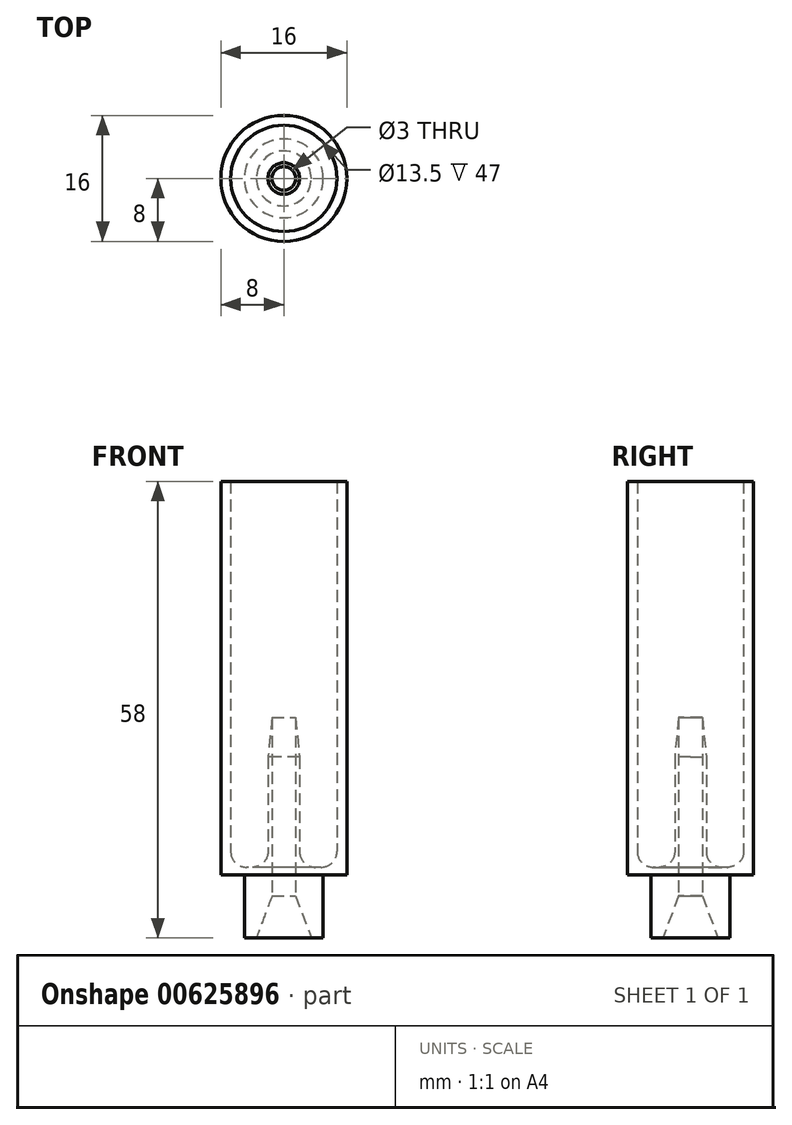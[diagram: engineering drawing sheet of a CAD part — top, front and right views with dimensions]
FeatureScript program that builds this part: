
annotation { "Feature Type Name" : "Feature", "Feature Type Description" : "" }
export const myFeature = defineFeature(function(context is Context, id is Id, definition is map)
    precondition{}
    {
        {
            var Q0;
            Q0=qCreatedBy(makeId("Top.planeOp"),FACE);
            var sketch = newSketch(context, id + "F0", { "sketchPlane" : qUnion([Q0])});
            skCircle(sketch, "E0", {"center": v(0, 0) * mm, "radius": 5 * mm});
            skCircle(sketch, "E1", {"center": v(0, 0) * mm, "radius": 3.5 * mm});
            skSolve(sketch);
        }
        {
            var Q0;
            Q0=makeQuery(id+"F0.imprint","IMPRINT",FACE,{"disambiguationData":[TD([[makeQuery(id+"F0.imprint","IMPRINT",EDGE,{"derivedFrom":sQuery(id+"F0.wireOp",EDGE,"E0")}),1.0]])]});
            extrude(context, id + "F1", {"entities" : qUnion([Q0]), "depth" : 8 * mm, "offsetDistance" : 25 * mm});
        }
        {
            var Q0;
            Q0=makeQuery(id+"F1.opExtrude","CAP_FACE",FACE,{"disambiguationData":[OSD([sQuery(id+"F0.wireOp",EDGE,"E0"),sQuery(id+"F0.wireOp",EDGE,"E1")])],"isStart":false});
            var sketch = newSketch(context, id + "F2", { "sketchPlane" : qUnion([Q0])});
            skCircle(sketch, "E2", {"center": v(0, 0) * mm, "radius": 8 * mm});
            skCircle(sketch, "E3", {"center": v(0, 0) * mm, "radius": 2 * mm});
            skCircle(sketch, "E4", {"center": v(0, 0) * mm, "radius": 1.5 * mm});
            skCircle(sketch, "E5", {"center": v(0, 0) * mm, "radius": 6.75 * mm});
            skSolve(sketch);
        }
        {
            var Q0;
            Q0 = qSketchRegion(id + "F2", true);
            var Q1;
            Q1=makeQuery(id+"F2.imprint","IMPRINT",FACE,{"disambiguationData":[TD([[makeQuery(id+"F2.imprint","IMPRINT",EDGE,{"derivedFrom":sQuery(id+"F2.wireOp",EDGE,"E5")}),1.0]])]});
            var Q2;
            Q2=makeQuery(id+"F2.imprint","IMPRINT",FACE,{"disambiguationData":[TD([[makeQuery(id+"F2.imprint","IMPRINT",EDGE,{"derivedFrom":makeQuery(id+"F1.opExtrude","CAP_EDGE",EDGE,{"disambiguationData":[OSD([sQuery(id+"F0.wireOp",EDGE,"E0")])],"isStart":false})}),1.0]])]});
            var Q3;
            Q3=makeQuery(id+"F2.imprint","IMPRINT",FACE,{"disambiguationData":[TD([[makeQuery(id+"F2.imprint","IMPRINT",EDGE,{"derivedFrom":sQuery(id+"F2.wireOp",EDGE,"E3")}),-1.0]])]});
            var Q4;
            Q4=makeQuery(id+"F2.imprint","IMPRINT",FACE,{"disambiguationData":[TD([[makeQuery(id+"F2.imprint","IMPRINT",EDGE,{"derivedFrom":sQuery(id+"F2.wireOp",EDGE,"E3")}),1.0]])]});
            extrude(context, id + "F3", {"entities" : qUnion([Q0, Q1, Q2, Q3, Q4]), "operationType" : NewBodyOperationType.ADD, "depth" : 1 * mm, "offsetDistance" : 25 * mm});
        }
        {
            var Q0;
            Q0 = qSketchRegion(id + "F2", true);
            extrude(context, id + "F4", {"entities" : qUnion([Q0]), "operationType" : NewBodyOperationType.ADD, "depth" : 50 * mm, "offsetDistance" : 25 * mm});
        }
        {
            var Q0;
            Q0=makeQuery(id+"F2.imprint","IMPRINT",FACE,{"disambiguationData":[TD([[makeQuery(id+"F2.imprint","IMPRINT",EDGE,{"derivedFrom":sQuery(id+"F2.wireOp",EDGE,"E3")}),1.0]])]});
            extrude(context, id + "F5", {"entities" : qUnion([Q0]), "operationType" : NewBodyOperationType.ADD, "depth" : 25 * mm, "offsetDistance" : 25 * mm});
        }
        {
            var Q0;
            Q0=makeQuery(id+"F1.opExtrude","CAP_EDGE",EDGE,{"disambiguationData":[OSD([sQuery(id+"F0.wireOp",EDGE,"E1")])],"isStart":false});
            chamfer(context, id + "F6", {"entities" : qUnion([Q0]), "chamferType" : ChamferType.TWO_OFFSETS, "width1" : 8 * mm, "oppositeDirection" : false, "width2" : 3 * mm, "tangentPropagation" : true});
        }
        {
            var Q0;
            Q0=makeQuery(id+"F5.boolean.opBoolean","INTERSECT",EDGE,{"derivedFrom":[makeQuery(id+"F3.opExtrude","CAP_FACE",FACE,{"disambiguationData":[OSD([sQuery(id+"F2.wireOp",EDGE,"E2"),sQuery(id+"F2.wireOp",EDGE,"E4")])],"isStart":false}),makeQuery(id+"F5.opExtrude","SWEPT_FACE",FACE,{"disambiguationData":[OSD([sQuery(id+"F2.wireOp",EDGE,"E3")])]})]});
            fillet(context, id + "F7", {"entities" : qUnion([Q0]), "radius" : 2 * mm, "tangentPropagation" : true, "allowEdgeOverflow" : false});
        }
        {
            var Q0;
            Q0=makeQuery(id+"F5.opExtrude","CAP_EDGE",EDGE,{"disambiguationData":[OSD([sQuery(id+"F2.wireOp",EDGE,"E3")])],"isStart":false});
            chamfer(context, id + "F8", {"entities" : qUnion([Q0]), "chamferType" : ChamferType.TWO_OFFSETS, "width1" : 1 * mm, "oppositeDirection" : false, "width2" : 10 * mm, "tangentPropagation" : true});
        }
        {
            var Q0;
            Q0=makeQuery(id+"F4.boolean.opBoolean","INTERSECT",EDGE,{"derivedFrom":[makeQuery(id+"F3.opExtrude","CAP_FACE",FACE,{"disambiguationData":[OSD([sQuery(id+"F2.wireOp",EDGE,"E2"),sQuery(id+"F2.wireOp",EDGE,"E4")])],"isStart":false}),makeQuery(id+"F4.opExtrude","SWEPT_FACE",FACE,{"disambiguationData":[OSD([sQuery(id+"F2.wireOp",EDGE,"E5")])]})]});
            fillet(context, id + "F9", {"entities" : qUnion([Q0]), "radius" : 2 * mm, "tangentPropagation" : true, "allowEdgeOverflow" : false});
        }
    });
